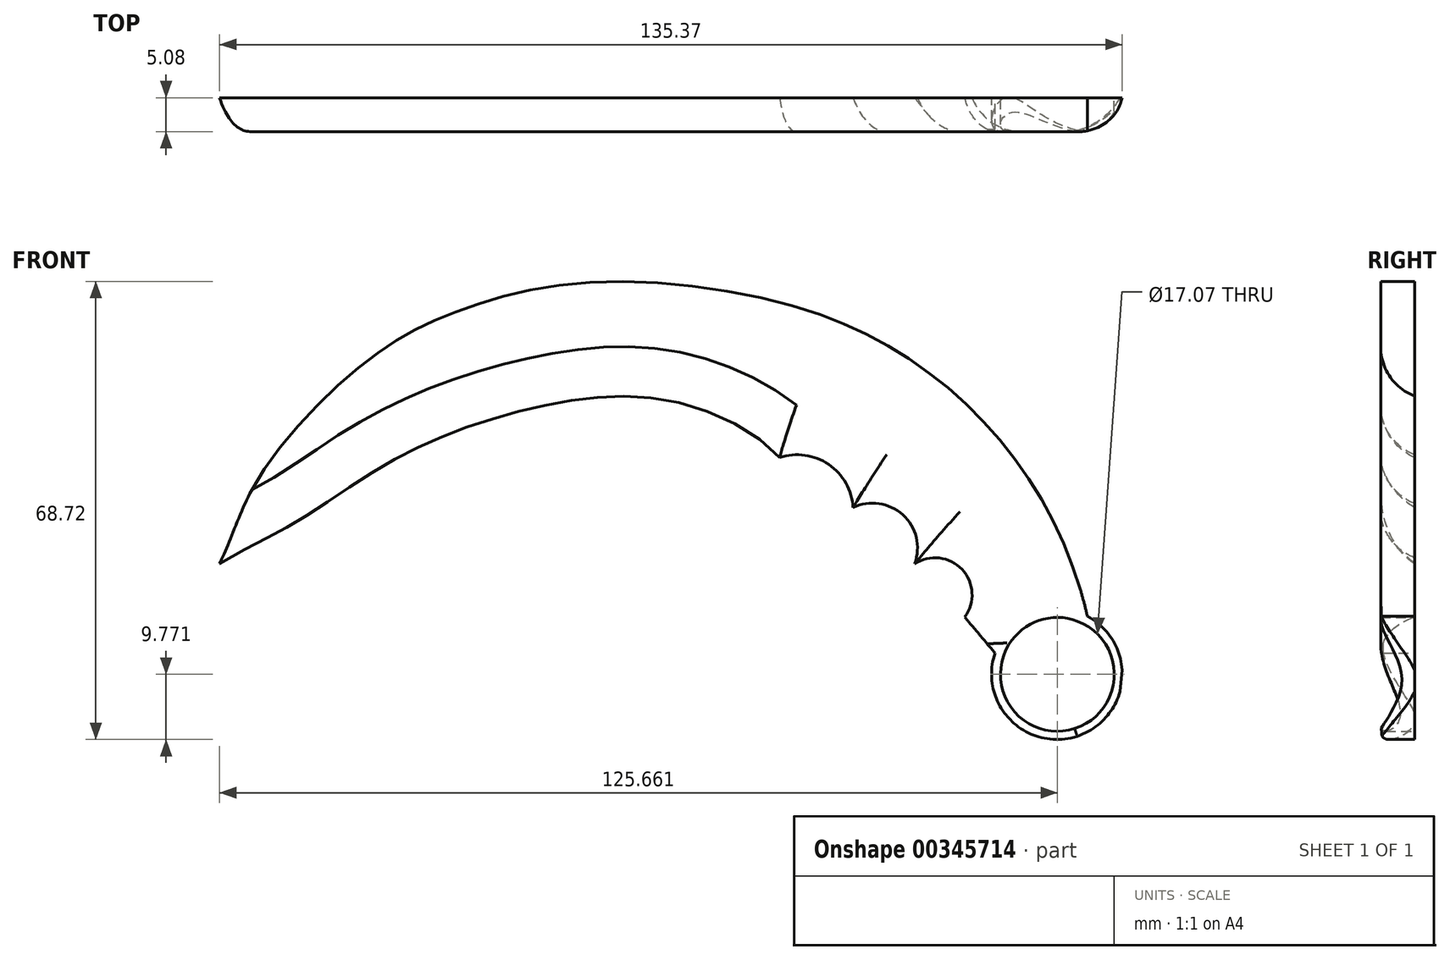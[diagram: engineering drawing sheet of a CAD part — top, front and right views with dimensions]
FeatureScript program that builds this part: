
annotation { "Feature Type Name" : "Feature", "Feature Type Description" : "" }
export const myFeature = defineFeature(function(context is Context, id is Id, definition is map)
    precondition{}
    {
        {
            var Q0;
            Q0=qCreatedBy(makeId("Front.planeOp"),FACE);
            var sketch = newSketch(context, id + "F0", { "sketchPlane" : qUnion([Q0])});
            skFitSpline(sketch, "E0", {"points": [v(-96.7, 0) * mm, v(-90.6, 13.3) * mm, v(-75.2, 29.93) * mm, v(-62.2, 37.42) * mm, v(-39.78, 42.3) * mm, v(-6.6, 37.4) * mm], "startDerivative": vector(37.97, 79.67) * mm, "endDerivative": vector(106.75, -37.65) * mm});
            skFitSpline(sketch, "E1", {"points": [v(-96.7, 0) * mm, v(-84.83, 6.5) * mm, v(-72.78, 14.35) * mm, v(-59.16, 20.64) * mm, v(-43.97, 24.48) * mm, v(-28.42, 24.3) * mm, v(-12.7, 15.92) * mm], "startDerivative": vector(95.86, 58.1) * mm, "endDerivative": vector(58.75, -67.56) * mm});
            skArc(sketch, "E2", {"start": v(-1.7, 8.41) * mm, "mid": v(-5.34, 14.9) * mm, "end": v(-12.7, 15.92) * mm});
            skArc(sketch, "E3", {"start": v(7.55, 0) * mm, "mid": v(5.77, 7.34) * mm, "end": v(-1.7, 8.41) * mm});
            skArc(sketch, "E4", {"start": v(15.06, -8) * mm, "mid": v(14.65, -0.86) * mm, "end": v(7.55, 0) * mm});
            skLineSegment(sketch, "E5", {"start": v(15.06, -8) * mm, "end": v(19.6, -13.41) * mm});
            skArc(sketch, "E6", {"start": v(33.4, -7.65) * mm, "mid": v(19.13, 19.97) * mm, "end": v(-6.6, 37.4) * mm});
            skCircle(sketch, "E7", {"center": v(28.88, -16.57) * mm, "radius": 9.8 * mm});
            skPoint(sketch, "E7.second.point", {"position": v(38.46, -18.65) * mm});
            skPoint(sketch, "E7.third.point", {"position": v(36.54, -10.45) * mm});
            skLineSegment(sketch, "E8", {"start": v(32.8, -5.32) * mm, "end": v(17.33, -10.7) * mm});
            skLineSegment(sketch, "E9", {"start": v(33.4, -7.65) * mm, "end": v(33.45, -7.9) * mm});
            skCircle(sketch, "E10", {"center": v(28.95, -16.6) * mm, "radius": 8.53 * mm});
            skPoint(sketch, "E10.first.point", {"position": v(22.06, -11.56) * mm});
            skPoint(sketch, "E10.second.point", {"position": v(35.57, -21.99) * mm});
            skPoint(sketch, "E10.third.point", {"position": v(37.07, -19.22) * mm});
            skLineSegment(sketch, "E11", {"start": v(21, -22.4) * mm, "end": v(36.27, -39.03) * mm});
            skLineSegment(sketch, "E12", {"start": v(36.27, -39.03) * mm, "end": v(38.66, -15.95) * mm});
            skSolve(sketch);
        }
        {
            var Q0;
            {var subQ0=sQuery(id+"F0.wireOp",EDGE,"E0");Q0=makeQuery(id+"F0.imprint","IMPRINT",FACE,{"disambiguationData":[TD([[makeQuery(id+"F0.imprint","IMPRINT",EDGE,{"derivedFrom":subQ0}),-1.0]])]});}
            var Q1;
            {var subQ0=sQuery(id+"F0.wireOp",EDGE,"E9");Q1=makeQuery(id+"F0.imprint","IMPRINT",FACE,{"disambiguationData":[TD([[makeQuery(id+"F0.imprint","IMPRINT",EDGE,{"derivedFrom":subQ0}),-1.0]])]});}
            var Q2;
            Q2=makeQuery(id+"F0.imprint","IMPRINT",FACE,{"disambiguationData":[TD([[makeQuery(id+"F0.imprint","IMPRINT",EDGE,{"derivedFrom":sQuery(id+"F0.wireOp",EDGE,"E10")}),-1.0]])]});
            var Q3;
            {var subQ0=sQuery(id+"F0.wireOp",EDGE,"E7");var subQ1=sQuery(id+"F0.wireOp",EDGE,"E5");var subQ2=makeQuery(id+"F0.imprint","INTERSECT",VERTEX,{"derivedFrom":[subQ1,subQ0]});Q3=makeQuery(id+"F0.imprint","IMPRINT",FACE,{"disambiguationData":[TD([[makeQuery(id+"F0.imprint","IMPRINT",EDGE,{"disambiguationData":[TD([[subQ2,1.0]])],"derivedFrom":subQ1}),1.0]])]});}
            var Q4;
            {var subQ0=sQuery(id+"F0.wireOp",EDGE,"E11");var subQ1=sQuery(id+"F0.wireOp",EDGE,"E7");var subQ2=makeQuery(id+"F0.imprint","INTERSECT",VERTEX,{"disambiguationData":[OD(1.0)],"derivedFrom":[subQ1,subQ0]});Q4=makeQuery(id+"F0.imprint","IMPRINT",FACE,{"disambiguationData":[TD([[makeQuery(id+"F0.imprint","IMPRINT",EDGE,{"disambiguationData":[TD([[subQ2,-1.0]])],"derivedFrom":subQ1}),-1.0]])]});}
            var Q5;
            {var subQ0=sQuery(id+"F0.wireOp",EDGE,"E8");var subQ1=sQuery(id+"F0.wireOp",EDGE,"E7");var subQ2=makeQuery(id+"F0.imprint","INTERSECT",VERTEX,{"disambiguationData":[OD(0.0)],"derivedFrom":[subQ1,subQ0]});Q5=makeQuery(id+"F0.imprint","IMPRINT",FACE,{"disambiguationData":[TD([[makeQuery(id+"F0.imprint","IMPRINT",EDGE,{"disambiguationData":[TD([[subQ2,-1.0]])],"derivedFrom":subQ1}),1.0]])]});}
            extrude(context, id + "F1", {"entities" : qUnion([Q0, Q1, Q2, Q3, Q4, Q5]), "endBound" : BoundingType.SYMMETRIC, "depth" : 5.08 * mm});
        }
        {
            var Q0;
            Q0=makeQuery(id+"F1.opExtrude","CAP_EDGE",EDGE,{"disambiguationData":[OSD([sQuery(id+"F0.wireOp",EDGE,"E1")])],"isStart":false});
            var Q1;
            Q1=makeQuery(id+"F1.opExtrude","CAP_EDGE",EDGE,{"disambiguationData":[OSD([sQuery(id+"F0.wireOp",EDGE,"E2")])],"isStart":false});
            var Q2;
            Q2=makeQuery(id+"F1.opExtrude","CAP_EDGE",EDGE,{"disambiguationData":[OSD([sQuery(id+"F0.wireOp",EDGE,"E3")])],"isStart":false});
            var Q3;
            Q3=makeQuery(id+"F1.opExtrude","CAP_EDGE",EDGE,{"disambiguationData":[OSD([sQuery(id+"F0.wireOp",EDGE,"E4")])],"isStart":false});
            var Q4;
            Q4=makeQuery(id+"F1.opExtrude","CAP_EDGE",EDGE,{"disambiguationData":[OSD([sQuery(id+"F0.wireOp",EDGE,"E11")])],"isStart":false});
            var Q5;
            Q5=makeQuery(id+"F1.opExtrude","CAP_EDGE",EDGE,{"disambiguationData":[OSD([sQuery(id+"F0.wireOp",EDGE,"E12")])],"isStart":false});
            fillet(context, id + "F2", {"entities" : qUnion([Q0, Q1, Q2, Q3, Q4, Q5]), "radius" : 7.97 * mm, "tangentPropagation" : true, "allowEdgeOverflow" : false});
        }
    });
